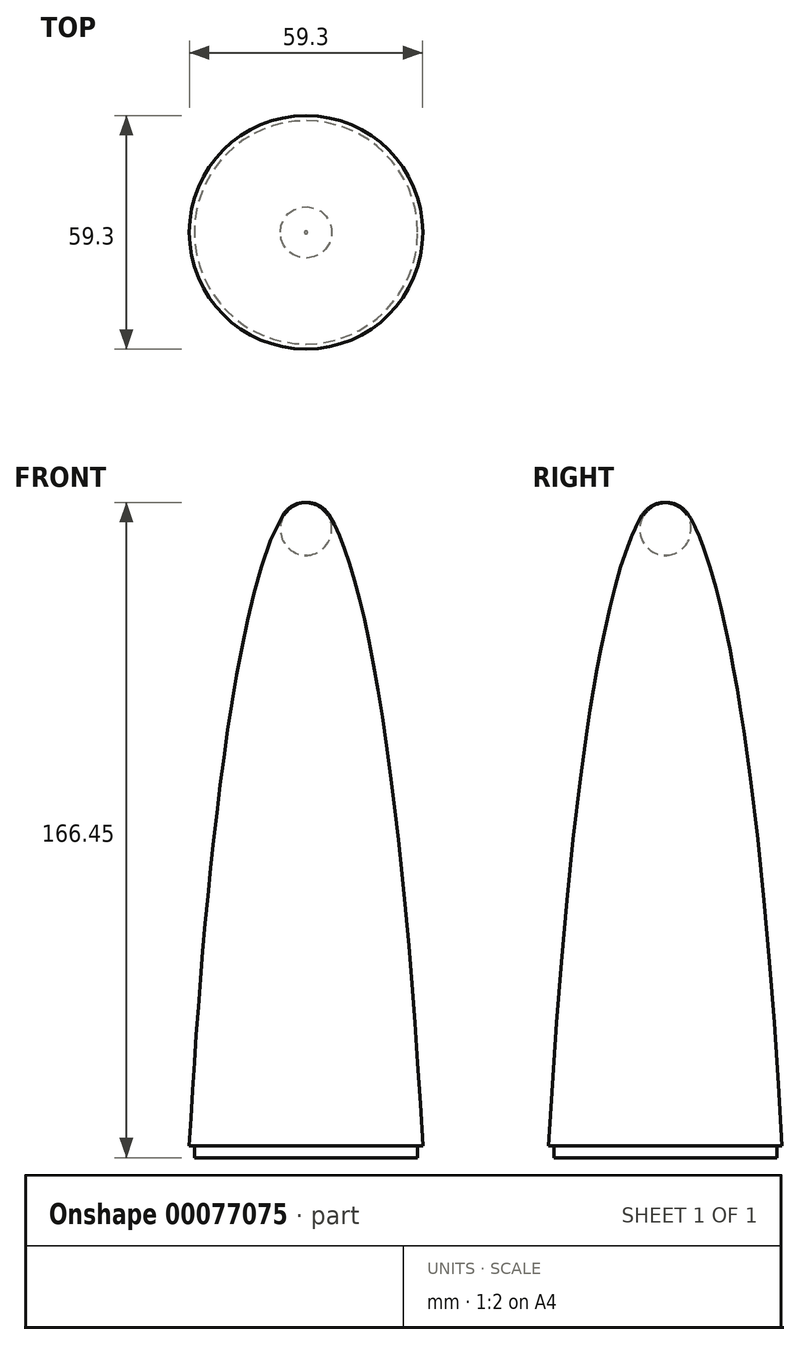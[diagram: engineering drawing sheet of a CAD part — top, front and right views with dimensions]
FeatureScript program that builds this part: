
annotation { "Feature Type Name" : "Feature", "Feature Type Description" : "" }
export const myFeature = defineFeature(function(context is Context, id is Id, definition is map)
    precondition{}
    {
        {
            var Q0;
            Q0=qCreatedBy(makeId("Front.planeOp"),FACE);
            var sketch = newSketch(context, id + "F0", { "sketchPlane" : qUnion([Q0])});
            skLineSegment(sketch, "E0", {"start": v(0, 294) * mm, "end": v(0, 129) * mm, "construction": true});
            skPoint(sketch, "E0.endSnap0", {"position": v(0, 294) * mm});
            skLineSegment(sketch, "E1.top", {"start": v(-28.36, 129) * mm, "end": v(-29.65, 129) * mm});
            skLineSegment(sketch, "E1.left", {"start": v(0, 294) * mm, "end": v(0, 129) * mm});
            skPoint(sketch, "E1.right.start.orphan", {"position": v(-63.28, 294) * mm});
            skPoint(sketch, "E2.orphan", {"position": v(-63.28, 129) * mm});
            skLineSegment(sketch, "E3.trimOffspring", {"start": v(0, 294) * mm, "end": v(0, -294) * mm, "construction": true});
            skLineSegment(sketch, "E4.trimOffspring", {"start": v(0, 129) * mm, "end": v(0, 294) * mm});
            skPoint(sketch, "E5.orphan", {"position": v(0, 67.2) * mm});
            skLineSegment(sketch, "E6.top", {"start": v(0, 126) * mm, "end": v(-28.36, 126) * mm});
            skLineSegment(sketch, "E6.left", {"start": v(0, 129) * mm, "end": v(0, 126) * mm});
            skLineSegment(sketch, "E6.right", {"start": v(-28.36, 129) * mm, "end": v(-28.36, 126) * mm});
            skEllipticalArc(sketch, "E7", {});
            skArc(sketch, "E8", {"start": v(-5.9, 289.26) * mm, "mid": v(-3.38, 291.64) * mm, "end": v(0, 292.45) * mm});
            const initialGuessF0  = {"E7": [0, 0, 0, 1, 0.294, 0.033, 0.17975226284269713, 1.1165607763701657]};
            skSetInitialGuess(sketch, initialGuessF0);
            skSolve(sketch);
        }
        {
            var Q0;
            Q0=makeQuery(id+"F0.imprint","IMPRINT",FACE,{"disambiguationData":[TD([[makeQuery(id+"F0.imprint","IMPRINT",EDGE,{"derivedFrom":sQuery(id+"F0.wireOp",EDGE,"E1.top")}),-1.0]])]});
            var Q1;
            Q1=sQuery(id+"F0.wireOp",EDGE,"E3.trimOffspring");
            revolve(context, id + "F1", {"entities" : qUnion([Q0]), "axis" : qUnion([Q1]), "revolveType" : RevolveType.FULL});
        }
        {
            var Q0;
            Q0=makeQuery(id+"F1.opRevolve","SWEPT_BODY",BODY,{"disambiguationData":[OSD([sQuery(id+"F0.wireOp",EDGE,"E1.top"),sQuery(id+"F0.wireOp",EDGE,"E4.trimOffspring"),sQuery(id+"F0.wireOp",EDGE,"E6.top"),sQuery(id+"F0.wireOp",EDGE,"E6.left"),sQuery(id+"F0.wireOp",EDGE,"E6.right"),sQuery(id+"F0.wireOp",EDGE,"E7"),sQuery(id+"F0.wireOp",EDGE,"E8")])]});
            transform(context, id + "F2", {"entities" : qUnion([Q0]), "transformType" : TransformType.TRANSLATION_3D, "dx" : 0 * mm, "dy" : 0 * mm, "dz" : -220 * mm, "makeCopy" : false});
        }
    });
